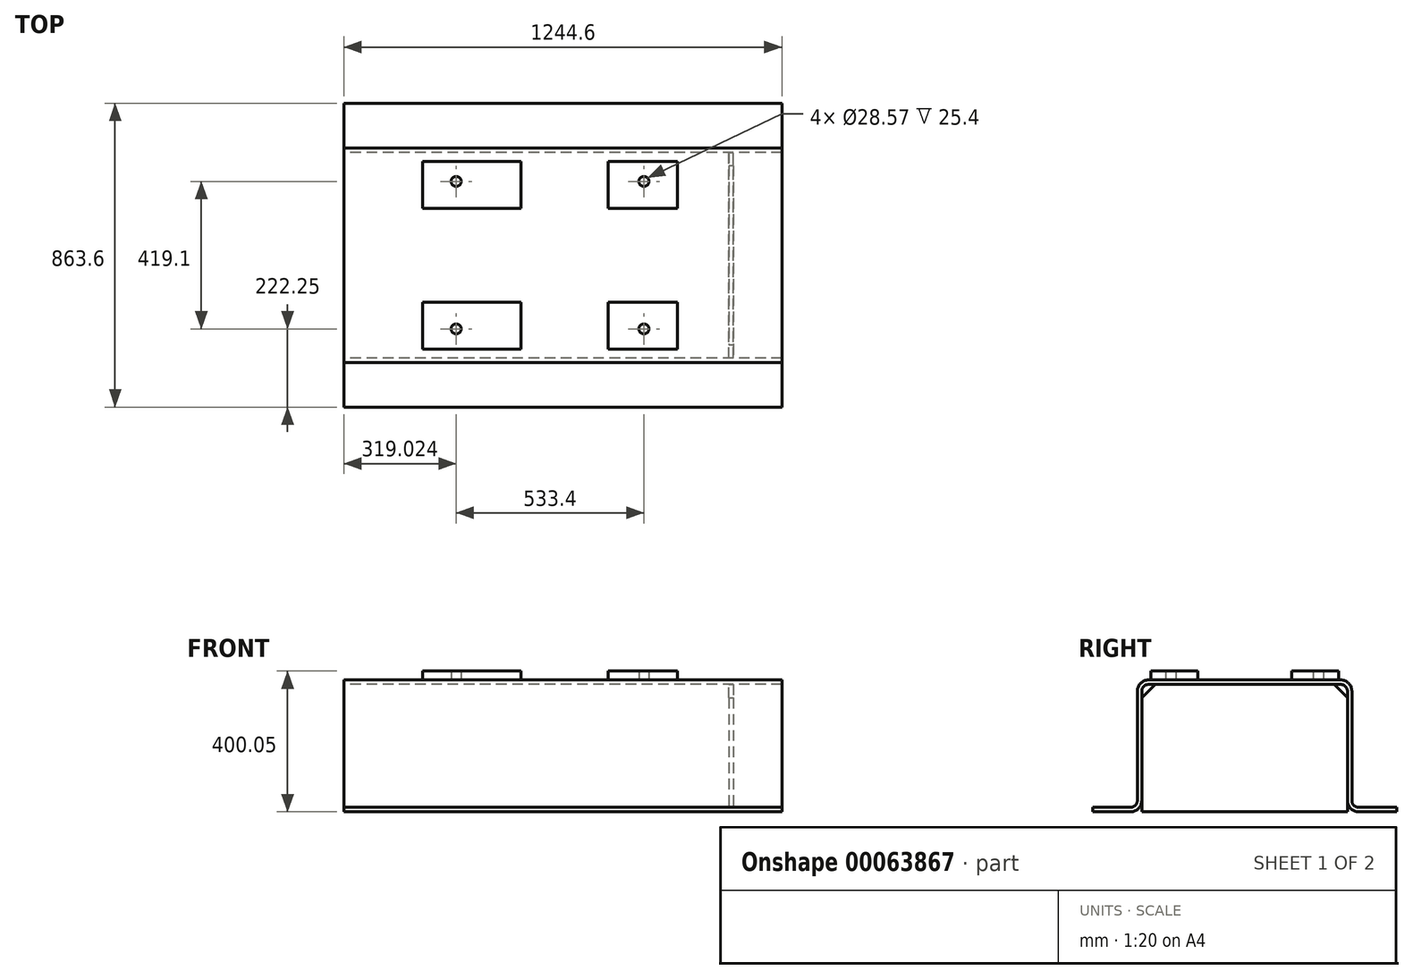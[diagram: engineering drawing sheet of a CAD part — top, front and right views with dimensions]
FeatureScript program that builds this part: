
annotation { "Feature Type Name" : "Feature", "Feature Type Description" : "" }
export const myFeature = defineFeature(function(context is Context, id is Id, definition is map)
    precondition{}
    {
        {
            var Q0;
            Q0=qCreatedBy(makeId("Right.planeOp"),FACE);
            var sketch = newSketch(context, id + "F0", { "sketchPlane" : qUnion([Q0])});
            skLineSegment(sketch, "E0", {"start": v(323.85, 0) * mm, "end": v(431.8, 0) * mm});
            skLineSegment(sketch, "E1", {"start": v(0, 389.85) * mm, "end": v(0, -350.8) * mm, "construction": true});
            skLineSegment(sketch, "E2.0", {"start": v(323.85, 12.7) * mm, "end": v(431.8, 12.7) * mm});
            skLineSegment(sketch, "E3.0", {"start": v(0, 374.65) * mm, "end": v(273.05, 374.65) * mm});
            skLineSegment(sketch, "E4.0", {"start": v(304.8, 342.9) * mm, "end": v(304.8, 31.75) * mm});
            skLineSegment(sketch, "E5.0", {"start": v(292.1, 342.9) * mm, "end": v(292.1, 31.75) * mm});
            skLineSegment(sketch, "E6.0", {"start": v(0, 361.95) * mm, "end": v(273.05, 361.95) * mm});
            skArc(sketch, "E7.filletArc", {"start": v(304.8, 31.75) * mm, "mid": v(310.38, 18.28) * mm, "end": v(323.85, 12.7) * mm});
            skArc(sketch, "E8.filletArc", {"start": v(292.1, 342.9) * mm, "mid": v(286.52, 356.37) * mm, "end": v(273.05, 361.95) * mm});
            skArc(sketch, "E9.filletArc", {"start": v(304.8, 342.9) * mm, "mid": v(295.5, 365.35) * mm, "end": v(273.05, 374.65) * mm});
            skPoint(sketch, "E10.newPointB", {"position": v(-431.8, 0) * mm});
            skArc(sketch, "E10.filletArc", {"start": v(292.1, 31.75) * mm, "mid": v(301.4, 9.3) * mm, "end": v(323.85, 0) * mm});
            skLineSegment(sketch, "E11", {"start": v(431.8, 12.7) * mm, "end": v(431.8, 0) * mm});
            skLineSegment(sketch, "E12.MirrorCS", {"start": v(-431.8, 12.7) * mm, "end": v(-431.8, 0) * mm});
            skArc(sketch, "E13.MirrorCS", {"start": v(-292.1, 342.9) * mm, "mid": v(-286.52, 356.37) * mm, "end": v(-273.05, 361.95) * mm});
            skArc(sketch, "E14.MirrorCS", {"start": v(-304.8, 31.75) * mm, "mid": v(-310.38, 18.28) * mm, "end": v(-323.85, 12.7) * mm});
            skArc(sketch, "E15.MirrorCS", {"start": v(-292.1, 31.75) * mm, "mid": v(-301.4, 9.3) * mm, "end": v(-323.85, 0) * mm});
            skLineSegment(sketch, "E16.MirrorCS", {"start": v(-323.85, 0) * mm, "end": v(-431.8, 0) * mm});
            skArc(sketch, "E17.MirrorCS", {"start": v(-304.8, 342.9) * mm, "mid": v(-295.5, 365.35) * mm, "end": v(-273.05, 374.65) * mm});
            skLineSegment(sketch, "E18.MirrorCS", {"start": v(0, 361.95) * mm, "end": v(-273.05, 361.95) * mm});
            skLineSegment(sketch, "E19.MirrorCS", {"start": v(-323.85, 12.7) * mm, "end": v(-431.8, 12.7) * mm});
            skLineSegment(sketch, "E20.MirrorCS", {"start": v(-292.1, 342.9) * mm, "end": v(-292.1, 31.75) * mm});
            skLineSegment(sketch, "E21.MirrorCS", {"start": v(0, 374.65) * mm, "end": v(-273.05, 374.65) * mm});
            skLineSegment(sketch, "E22.MirrorCS", {"start": v(-304.8, 342.9) * mm, "end": v(-304.8, 31.75) * mm});
            skSolve(sketch);
        }
        {
            var Q0;
            Q0 = qSketchRegion(id + "F0", true);
            extrude(context, id + "F1", {"entities" : qUnion([Q0]), "endBound" : BoundingType.SYMMETRIC, "depth" : 1244.6 * mm});
        }
        {
            var Q0;
            Q0=makeQuery(id+"F1.opExtrude","SWEPT_FACE",FACE,{"disambiguationData":[OSD([sQuery(id+"F0.wireOp",EDGE,"E3.0"),sQuery(id+"F0.wireOp",EDGE,"E21.MirrorCS")])]});
            var sketch = newSketch(context, id + "F2", { "sketchPlane" : qUnion([Q0])});
            skLineSegment(sketch, "E23.0", {"start": v(622.3, -273.05) * mm, "end": v(622.3, 273.05) * mm, "construction": true});
            skSolve(sketch);
        }
        {
            var Q0;
            {var subQ0=sQuery(id+"F0.wireOp",EDGE,"E3.0");Q0=makeQuery(id+"F2.imprint","IMPRINT",FACE,{"disambiguationData":[TD([[makeQuery(id+"F2.imprint","IMPRINT",EDGE,{"derivedFrom":makeQuery(id+"F1.opExtrude","SWEPT_EDGE",EDGE,{"disambiguationData":[OSD([subQ0,sQuery(id+"F0.wireOp",EDGE,"E9.filletArc")])]})}),1.0]])]});}
            var sketch = newSketch(context, id + "F3", { "sketchPlane" : qUnion([Q0])});
            skLineSegment(sketch, "E24.0", {"start": v(622.3, -273.05) * mm, "end": v(622.3, 273.05) * mm, "construction": true});
            skLineSegment(sketch, "E25", {"start": v(-721.27, 0) * mm, "end": v(806.54, 0) * mm, "construction": true});
            skLineSegment(sketch, "E26.0", {"start": v(477.77, -273.05) * mm, "end": v(477.77, 273.05) * mm, "construction": true});
            skLineSegment(sketch, "E27.0", {"start": v(-36.58, -273.05) * mm, "end": v(-36.58, 273.05) * mm, "construction": true});
            skLineSegment(sketch, "E28.0", {"start": v(128.52, -273.05) * mm, "end": v(128.52, 273.05) * mm, "construction": true});
            skLineSegment(sketch, "E29.0", {"start": v(325.37, -273.05) * mm, "end": v(325.37, 273.05) * mm, "construction": true});
            skLineSegment(sketch, "E30.0", {"start": v(-721.27, -133.35) * mm, "end": v(806.54, -133.35) * mm, "construction": true});
            skLineSegment(sketch, "E31.0", {"start": v(-721.27, -266.7) * mm, "end": v(806.54, -266.7) * mm, "construction": true});
            skLineSegment(sketch, "E32.bottom", {"start": v(128.52, -133.35) * mm, "end": v(325.37, -133.35) * mm});
            skLineSegment(sketch, "E32.top", {"start": v(128.52, -266.7) * mm, "end": v(325.37, -266.7) * mm});
            skLineSegment(sketch, "E32.left", {"start": v(128.52, -133.35) * mm, "end": v(128.52, -266.7) * mm});
            skLineSegment(sketch, "E32.right", {"start": v(325.37, -133.35) * mm, "end": v(325.37, -266.7) * mm});
            skLineSegment(sketch, "E33.0", {"start": v(-119.13, -273.05) * mm, "end": v(-119.13, 273.05) * mm, "construction": true});
            skLineSegment(sketch, "E34.bottom", {"start": v(-119.13, -266.7) * mm, "end": v(-398.53, -266.7) * mm});
            skLineSegment(sketch, "E34.top", {"start": v(-119.13, -133.35) * mm, "end": v(-398.53, -133.35) * mm});
            skLineSegment(sketch, "E34.left", {"start": v(-119.13, -266.7) * mm, "end": v(-119.13, -133.35) * mm});
            skLineSegment(sketch, "E34.right", {"start": v(-398.53, -266.7) * mm, "end": v(-398.53, -133.35) * mm});
            skLineSegment(sketch, "E35.0", {"start": v(-303.28, -273.05) * mm, "end": v(-303.28, 273.05) * mm, "construction": true});
            skLineSegment(sketch, "E36.0", {"start": v(230.12, -273.05) * mm, "end": v(230.12, 273.05) * mm, "construction": true});
            skLineSegment(sketch, "E37.0", {"start": v(-721.27, -209.55) * mm, "end": v(806.54, -209.55) * mm, "construction": true});
            skCircle(sketch, "E38", {"center": v(-303.28, -209.55) * mm, "radius": 14.29 * mm});
            skCircle(sketch, "E39", {"center": v(230.12, -209.55) * mm, "radius": 14.29 * mm});
            skCircle(sketch, "E40.MirrorC", {"center": v(-303.28, 209.55) * mm, "radius": 14.29 * mm});
            skCircle(sketch, "E41.MirrorC", {"center": v(230.12, 209.55) * mm, "radius": 14.29 * mm});
            skLineSegment(sketch, "E42.MirrorCS", {"start": v(-119.13, 266.7) * mm, "end": v(-398.53, 266.7) * mm});
            skLineSegment(sketch, "E43.MirrorCS", {"start": v(-119.13, 133.35) * mm, "end": v(-398.53, 133.35) * mm});
            skLineSegment(sketch, "E44.MirrorCS", {"start": v(-119.13, 266.7) * mm, "end": v(-119.13, 133.35) * mm});
            skLineSegment(sketch, "E45.MirrorCS", {"start": v(-398.53, 266.7) * mm, "end": v(-398.53, 133.35) * mm});
            skLineSegment(sketch, "E46.MirrorCS", {"start": v(325.37, 133.35) * mm, "end": v(325.37, 266.7) * mm});
            skLineSegment(sketch, "E47.MirrorCS", {"start": v(128.52, 133.35) * mm, "end": v(325.37, 133.35) * mm});
            skLineSegment(sketch, "E48.MirrorCS", {"start": v(128.52, 133.35) * mm, "end": v(128.52, 266.7) * mm});
            skLineSegment(sketch, "E49.MirrorCS", {"start": v(128.52, 266.7) * mm, "end": v(325.37, 266.7) * mm});
            skSolve(sketch);
        }
        {
            var Q0;
            Q0 = qSketchRegion(id + "F3", true);
            extrude(context, id + "F4", {"entities" : qUnion([Q0]), "operationType" : NewBodyOperationType.ADD, "depth" : 25.4 * mm});
        }
        {
            var Q0;
            Q0=makeQuery(id+"F1.opExtrude","SWEPT_FACE",FACE,{"disambiguationData":[OSD([sQuery(id+"F0.wireOp",EDGE,"E0")])]});
            var sketch = newSketch(context, id + "F5", { "sketchPlane" : qUnion([Q0])});
            skLineSegment(sketch, "E50.0", {"start": v(477.77, 273.05) * mm, "end": v(477.77, -273.05) * mm, "construction": true});
            skLineSegment(sketch, "E51.0.1", {"start": v(-622.3, -292.1) * mm, "end": v(622.3, -292.1) * mm, "construction": true});
            skLineSegment(sketch, "E51.0.3", {"start": v(622.3, -292.1) * mm, "end": v(-622.3, -292.1) * mm, "construction": true});
            skLineSegment(sketch, "E52.0.1", {"start": v(-622.3, 292.1) * mm, "end": v(622.3, 292.1) * mm, "construction": true});
            skLineSegment(sketch, "E52.0.3", {"start": v(622.3, 292.1) * mm, "end": v(-622.3, 292.1) * mm, "construction": true});
            skLineSegment(sketch, "E53.0", {"start": v(484.12, 292.1) * mm, "end": v(484.12, -292.1) * mm});
            skLineSegment(sketch, "E54.bottom", {"start": v(484.12, 292.1) * mm, "end": v(471.42, 292.1) * mm});
            skLineSegment(sketch, "E54.top", {"start": v(484.12, -292.1) * mm, "end": v(471.42, -292.1) * mm});
            skLineSegment(sketch, "E54.right", {"start": v(471.42, 292.1) * mm, "end": v(471.42, -292.1) * mm});
            skSolve(sketch);
        }
        {
            var Q0;
            Q0 = qSketchRegion(id + "F5", true);
            var Q1;
            Q1=makeQuery(id+"F1.opExtrude","SWEPT_FACE",FACE,{"disambiguationData":[OSD([sQuery(id+"F0.wireOp",EDGE,"E6.0"),sQuery(id+"F0.wireOp",EDGE,"E18.MirrorCS")])]});
            extrude(context, id + "F6", {"entities" : qUnion([Q0]), "endBound" : BoundingType.UP_TO_SURFACE, "oppositeDirection" : true, "endBoundEntityFace" : qUnion([Q1]), "depth" : 25.4 * mm});
        }
        {
            var Q0;
            Q0=makeQuery(id+"F6.opExtrude","CAP_EDGE",EDGE,{"disambiguationData":[OSD([sQuery(id+"F5.wireOp",EDGE,"E54.bottom")])],"isStart":false});
            var Q1;
            Q1=makeQuery(id+"F6.opExtrude","CAP_EDGE",EDGE,{"disambiguationData":[OSD([sQuery(id+"F5.wireOp",EDGE,"E54.top")])],"isStart":false});
            chamfer(context, id + "F7", {"entities" : qUnion([Q0, Q1]), "width" : 38.1 * mm, "tangentPropagation" : true});
        }
    });
